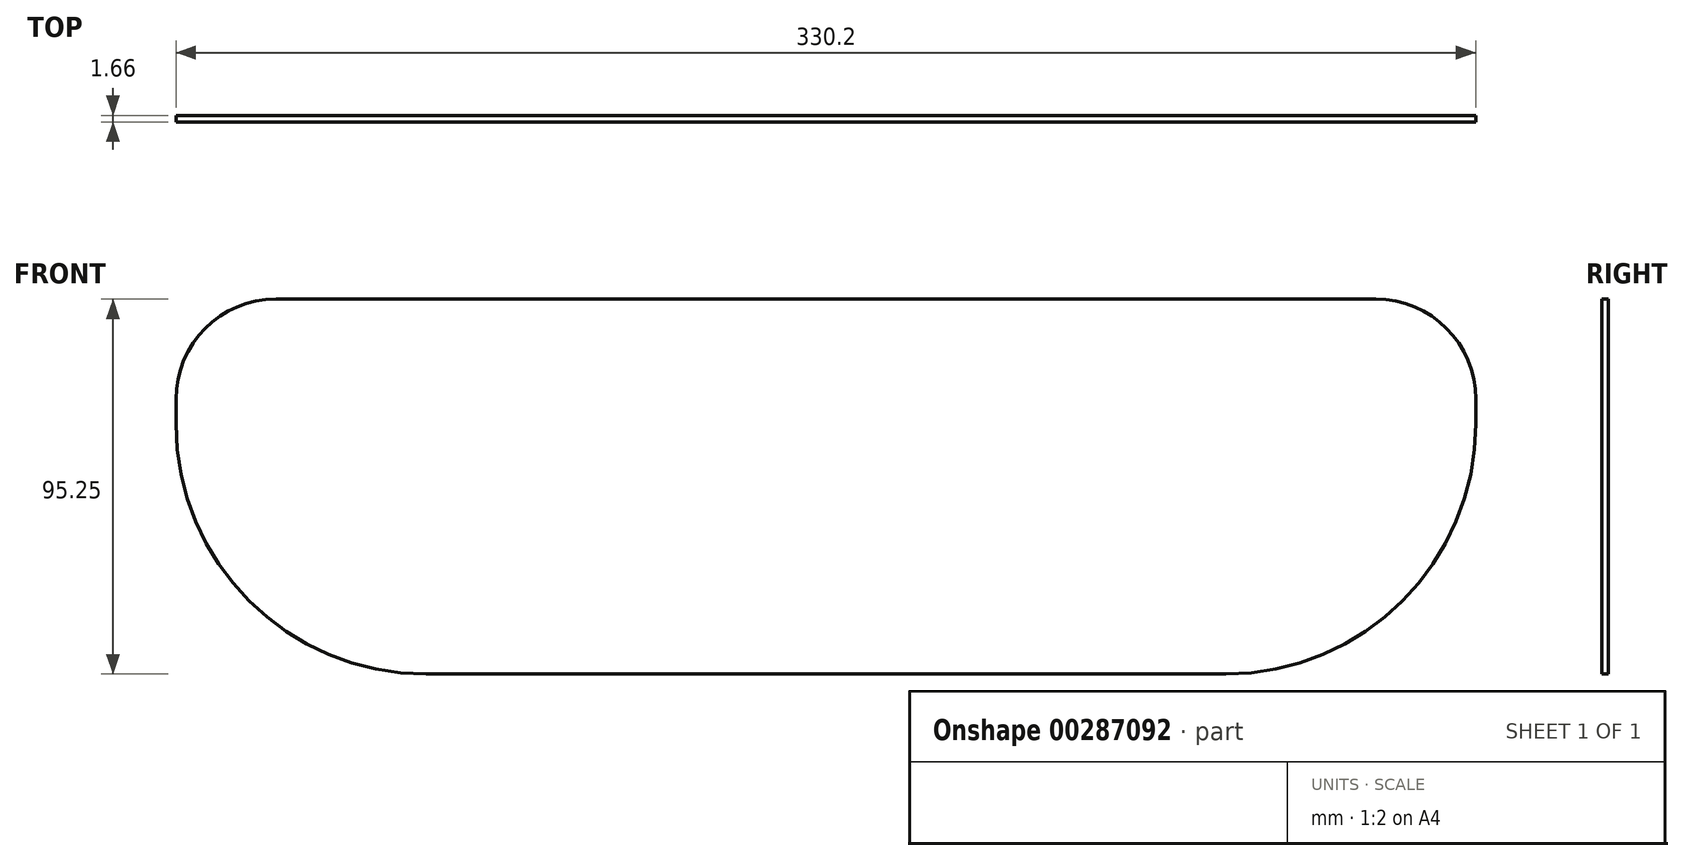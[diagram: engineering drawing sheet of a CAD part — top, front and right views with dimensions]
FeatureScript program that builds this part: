
annotation { "Feature Type Name" : "Feature", "Feature Type Description" : "" }
export const myFeature = defineFeature(function(context is Context, id is Id, definition is map)
    precondition{}
    {
        {
            var Q0;
            Q0=qCreatedBy(makeId("Front.planeOp"),FACE);
            var sketch = newSketch(context, id + "F0", { "sketchPlane" : qUnion([Q0])});
            skLineSegment(sketch, "E0", {"start": v(0, 47.63) * mm, "end": v(0, -47.62) * mm});
            skLineSegment(sketch, "E1", {"start": v(0, 47.63) * mm, "end": v(139.7, 47.63) * mm});
            skLineSegment(sketch, "E2", {"start": v(0, -47.62) * mm, "end": v(101.6, -47.62) * mm});
            skLineSegment(sketch, "E3", {"start": v(165.1, 15.88) * mm, "end": v(165.1, 22.23) * mm});
            skPoint(sketch, "E4.visualSharp", {"position": v(165.1, 47.63) * mm});
            skArc(sketch, "E4.filletArc", {"start": v(165.1, 22.23) * mm, "mid": v(157.66, 40.19) * mm, "end": v(139.7, 47.63) * mm});
            skPoint(sketch, "E5.first.point", {"position": v(286.64, 47.63) * mm});
            skPoint(sketch, "E5.second.point", {"position": v(165.1, 0) * mm});
            skPoint(sketch, "E5.third.point", {"position": v(285.87, -47.62) * mm});
            skArc(sketch, "E6.trimOffspring", {"start": v(165.1, 0) * mm, "mid": v(165.1, 0) * mm, "end": v(165.1, 0) * mm});
            skPoint(sketch, "E7.visualSharp", {"position": v(165.1, -47.62) * mm});
            skArc(sketch, "E7.filletArc", {"start": v(101.6, -47.62) * mm, "mid": v(146.5, -29.03) * mm, "end": v(165.1, 15.88) * mm});
            skSolve(sketch);
        }
        {
            var Q0;
            Q0=makeQuery(id+"F0.imprint","IMPRINT",FACE,{"disambiguationData":[TD([[makeQuery(id+"F0.imprint","IMPRINT",EDGE,{"derivedFrom":sQuery(id+"F0.wireOp",EDGE,"E0")}),1.0]])]});
            extrude(context, id + "F1", {"entities" : qUnion([Q0]), "endBound" : BoundingType.SYMMETRIC, "depth" : 1.65 * mm});
        }
        {
            var Q0;
            Q0=makeQuery(id+"F1.opExtrude","SWEPT_BODY",BODY,{"disambiguationData":[OSD([sQuery(id+"F0.wireOp",EDGE,"E0"),sQuery(id+"F0.wireOp",EDGE,"E1"),sQuery(id+"F0.wireOp",EDGE,"E2"),sQuery(id+"F0.wireOp",EDGE,"E3"),sQuery(id+"F0.wireOp",EDGE,"E4.filletArc"),sQuery(id+"F0.wireOp",EDGE,"E7.filletArc")])]});
            var Q1;
            Q1=qCreatedBy(makeId("Right.planeOp"),FACE);
            mirror(context, id + "F2", {"operationType" : NewBodyOperationType.ADD, "entities" : qUnion([Q0]), "mirrorPlane" : qUnion([Q1])});
        }
    });
